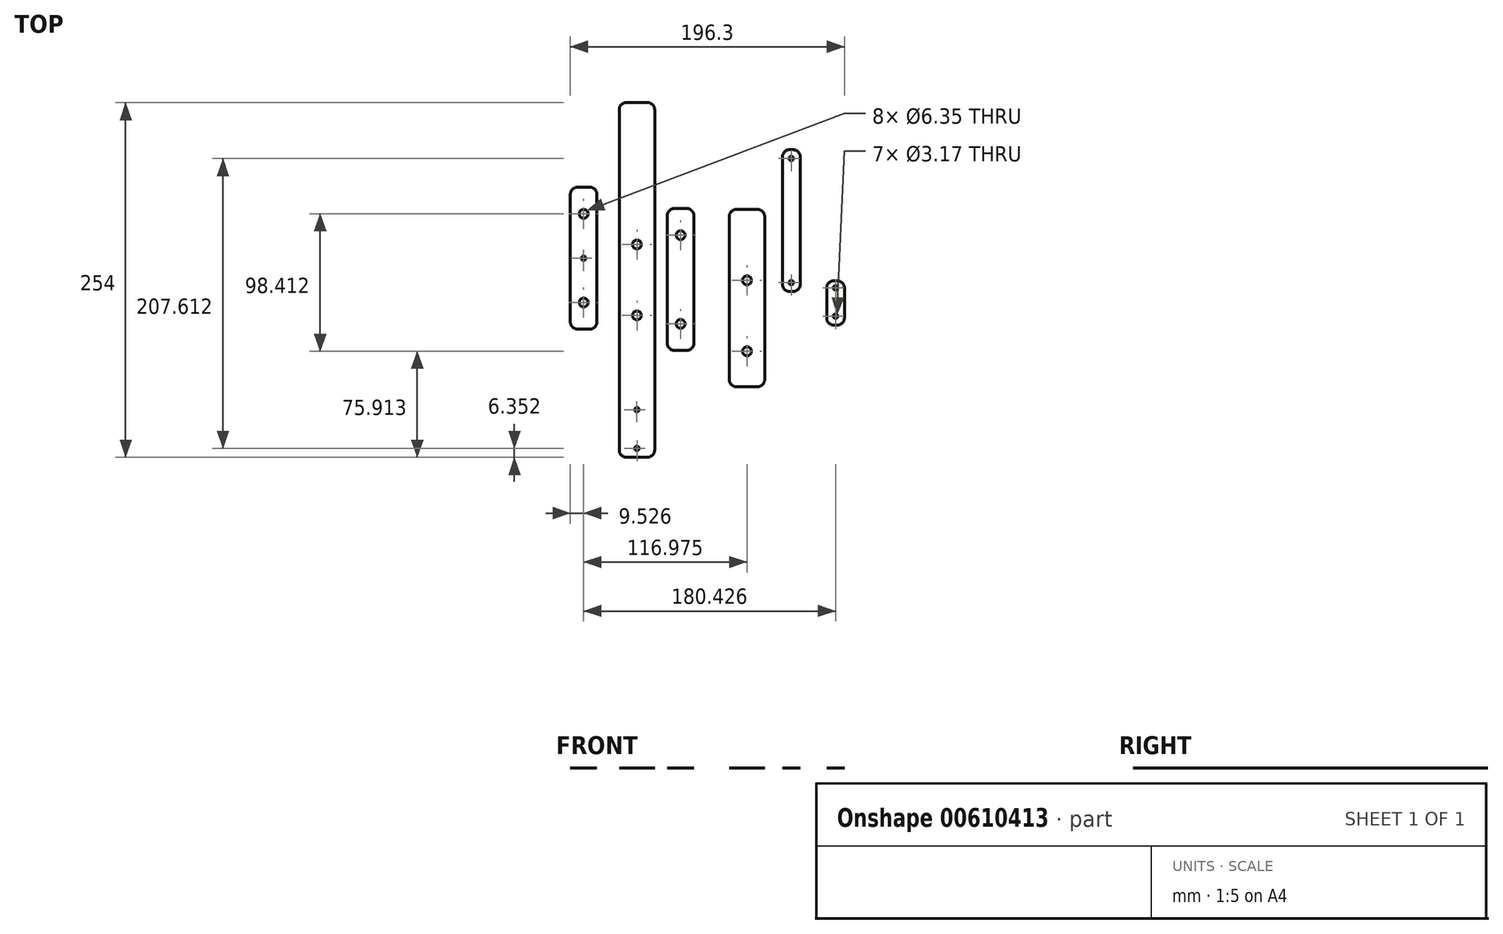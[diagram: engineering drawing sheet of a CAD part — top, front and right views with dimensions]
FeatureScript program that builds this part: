
annotation { "Feature Type Name" : "Feature", "Feature Type Description" : "" }
export const myFeature = defineFeature(function(context is Context, id is Id, definition is map)
    precondition{}
    {
        {
            var Q0;
            Q0=qCreatedBy(makeId("Top.planeOp"),FACE);
            var sketch = newSketch(context, id + "F0", { "sketchPlane" : qUnion([Q0])});
            skLineSegment(sketch, "E0.bottom", {"start": v(-140.54, 177.2) * mm, "end": v(-125.3, 177.2) * mm});
            skLineSegment(sketch, "E0.top", {"start": v(-140.54, -76.8) * mm, "end": v(-125.3, -76.8) * mm});
            skLineSegment(sketch, "E0.left", {"start": v(-145.62, 172.12) * mm, "end": v(-145.62, -71.72) * mm});
            skLineSegment(sketch, "E0.right", {"start": v(-120.22, 172.12) * mm, "end": v(-120.22, -71.72) * mm});
            skCircle(sketch, "E1", {"center": v(-132.92, 24.8) * mm, "radius": 3.18 * mm});
            skCircle(sketch, "E2", {"center": v(-132.92, 75.6) * mm, "radius": 3.18 * mm});
            skCircle(sketch, "E3", {"center": v(-132.92, -70.45) * mm, "radius": 1.59 * mm});
            skPoint(sketch, "E3.centerSnap0", {"position": v(-132.92, -76.8) * mm});
            skCircle(sketch, "E4", {"center": v(-132.95, -42.69) * mm, "radius": 1.59 * mm});
            skPoint(sketch, "E5.visualSharp", {"position": v(-145.62, 177.2) * mm});
            skArc(sketch, "E5.filletArc", {"start": v(-140.54, 177.2) * mm, "mid": v(-144.14, 175.71) * mm, "end": v(-145.62, 172.12) * mm});
            skPoint(sketch, "E6.visualSharp", {"position": v(-120.22, 177.2) * mm});
            skArc(sketch, "E6.filletArc", {"start": v(-120.22, 172.12) * mm, "mid": v(-121.71, 175.71) * mm, "end": v(-125.3, 177.2) * mm});
            skPoint(sketch, "E7.visualSharp", {"position": v(-145.62, -76.8) * mm});
            skArc(sketch, "E7.filletArc", {"start": v(-145.62, -71.72) * mm, "mid": v(-144.14, -75.31) * mm, "end": v(-140.54, -76.8) * mm});
            skPoint(sketch, "E8.visualSharp", {"position": v(-120.22, -76.8) * mm});
            skArc(sketch, "E8.filletArc", {"start": v(-125.3, -76.8) * mm, "mid": v(-121.71, -75.31) * mm, "end": v(-120.22, -71.72) * mm});
            skSolve(sketch);
        }
        {
            var Q0;
            Q0=qCreatedBy(makeId("Top.planeOp"),FACE);
            var sketch = newSketch(context, id + "F1", { "sketchPlane" : qUnion([Q0])});
            skLineSegment(sketch, "E9.bottom", {"start": v(-61.74, 100.71) * mm, "end": v(-46.5, 100.71) * mm});
            skLineSegment(sketch, "E9.top", {"start": v(-61.74, -26.29) * mm, "end": v(-46.5, -26.29) * mm});
            skLineSegment(sketch, "E9.left", {"start": v(-66.82, 95.63) * mm, "end": v(-66.82, -21.2) * mm});
            skLineSegment(sketch, "E9.right", {"start": v(-41.42, 95.63) * mm, "end": v(-41.42, -21.2) * mm});
            skCircle(sketch, "E10", {"center": v(-54.12, 49.91) * mm, "radius": 3.18 * mm});
            skCircle(sketch, "E11", {"center": v(-54.12, -0.89) * mm, "radius": 3.18 * mm});
            skPoint(sketch, "E12.visualSharp", {"position": v(-66.82, 100.71) * mm});
            skArc(sketch, "E12.filletArc", {"start": v(-61.74, 100.71) * mm, "mid": v(-65.33, 99.23) * mm, "end": v(-66.82, 95.63) * mm});
            skPoint(sketch, "E13.visualSharp", {"position": v(-41.42, 100.71) * mm});
            skArc(sketch, "E13.filletArc", {"start": v(-41.42, 95.63) * mm, "mid": v(-42.9, 99.23) * mm, "end": v(-46.5, 100.71) * mm});
            skPoint(sketch, "E14.visualSharp", {"position": v(-66.82, -26.29) * mm});
            skArc(sketch, "E14.filletArc", {"start": v(-66.82, -21.2) * mm, "mid": v(-65.33, -24.8) * mm, "end": v(-61.74, -26.29) * mm});
            skPoint(sketch, "E15.visualSharp", {"position": v(-41.42, -26.29) * mm});
            skArc(sketch, "E15.filletArc", {"start": v(-46.5, -26.29) * mm, "mid": v(-42.9, -24.8) * mm, "end": v(-41.42, -21.2) * mm});
            skSolve(sketch);
        }
        {
            var Q0;
            Q0=qCreatedBy(makeId("Top.planeOp"),FACE);
            var sketch = newSketch(context, id + "F2", { "sketchPlane" : qUnion([Q0])});
            skLineSegment(sketch, "E16.bottom", {"start": v(-106.08, 101.31) * mm, "end": v(-97.19, 101.31) * mm});
            skLineSegment(sketch, "E16.top", {"start": v(-106.08, -0.29) * mm, "end": v(-97.19, -0.29) * mm});
            skLineSegment(sketch, "E16.left", {"start": v(-111.16, 96.23) * mm, "end": v(-111.16, 4.8) * mm});
            skLineSegment(sketch, "E16.right", {"start": v(-92.1, 96.23) * mm, "end": v(-92.1, 4.8) * mm});
            skCircle(sketch, "E17", {"center": v(-101.63, 82.26) * mm, "radius": 3.18 * mm});
            skCircle(sketch, "E18", {"center": v(-101.63, 18.76) * mm, "radius": 3.18 * mm});
            skPoint(sketch, "E19.visualSharp", {"position": v(-111.16, 101.31) * mm});
            skArc(sketch, "E19.filletArc", {"start": v(-106.08, 101.31) * mm, "mid": v(-109.67, 99.83) * mm, "end": v(-111.16, 96.23) * mm});
            skPoint(sketch, "E20.visualSharp", {"position": v(-92.1, 101.31) * mm});
            skArc(sketch, "E20.filletArc", {"start": v(-92.1, 96.23) * mm, "mid": v(-93.6, 99.83) * mm, "end": v(-97.19, 101.31) * mm});
            skPoint(sketch, "E21.visualSharp", {"position": v(-111.16, -0.29) * mm});
            skArc(sketch, "E21.filletArc", {"start": v(-111.16, 4.8) * mm, "mid": v(-109.67, 1.2) * mm, "end": v(-106.08, -0.29) * mm});
            skPoint(sketch, "E22.visualSharp", {"position": v(-92.1, -0.29) * mm});
            skArc(sketch, "E22.filletArc", {"start": v(-97.19, -0.29) * mm, "mid": v(-93.6, 1.2) * mm, "end": v(-92.1, 4.8) * mm});
            skSolve(sketch);
        }
        {
            var Q0;
            Q0=qCreatedBy(makeId("Top.planeOp"),FACE);
            var sketch = newSketch(context, id + "F3", { "sketchPlane" : qUnion([Q0])});
            skLineSegment(sketch, "E23.bottom", {"start": v(-23.62, 143.51) * mm, "end": v(-21.08, 143.51) * mm});
            skLineSegment(sketch, "E23.top", {"start": v(-23.62, 41.91) * mm, "end": v(-21.08, 41.91) * mm});
            skLineSegment(sketch, "E23.left", {"start": v(-28.7, 138.43) * mm, "end": v(-28.7, 47) * mm});
            skLineSegment(sketch, "E23.right", {"start": v(-16, 138.43) * mm, "end": v(-16, 47) * mm});
            skCircle(sketch, "E24", {"center": v(-22.35, 48.26) * mm, "radius": 1.59 * mm});
            skCircle(sketch, "E25", {"center": v(-22.35, 137.16) * mm, "radius": 1.59 * mm});
            skPoint(sketch, "E26.visualSharp", {"position": v(-28.7, 143.51) * mm});
            skArc(sketch, "E26.filletArc", {"start": v(-23.62, 143.51) * mm, "mid": v(-27.2, 142.03) * mm, "end": v(-28.7, 138.43) * mm});
            skPoint(sketch, "E27.visualSharp", {"position": v(-16, 143.51) * mm});
            skArc(sketch, "E27.filletArc", {"start": v(-16, 138.43) * mm, "mid": v(-17.48, 142.03) * mm, "end": v(-21.08, 143.51) * mm});
            skPoint(sketch, "E28.visualSharp", {"position": v(-28.7, 41.91) * mm});
            skArc(sketch, "E28.filletArc", {"start": v(-28.7, 47) * mm, "mid": v(-27.2, 43.4) * mm, "end": v(-23.62, 41.91) * mm});
            skPoint(sketch, "E29.visualSharp", {"position": v(-16, 41.91) * mm});
            skArc(sketch, "E29.filletArc", {"start": v(-21.08, 41.91) * mm, "mid": v(-17.48, 43.4) * mm, "end": v(-16, 47) * mm});
            skSolve(sketch);
        }
        {
            var Q0;
            Q0=qCreatedBy(makeId("Top.planeOp"),FACE);
            var sketch = newSketch(context, id + "F4", { "sketchPlane" : qUnion([Q0])});
            skLineSegment(sketch, "E30.bottom", {"start": v(-175.54, 116.57) * mm, "end": v(-166.65, 116.57) * mm});
            skLineSegment(sketch, "E30.top", {"start": v(-175.54, 14.97) * mm, "end": v(-166.65, 14.97) * mm});
            skLineSegment(sketch, "E30.left", {"start": v(-180.62, 111.5) * mm, "end": v(-180.62, 20.05) * mm});
            skLineSegment(sketch, "E30.right", {"start": v(-161.57, 111.5) * mm, "end": v(-161.57, 20.05) * mm});
            skCircle(sketch, "E31", {"center": v(-171.1, 97.52) * mm, "radius": 3.18 * mm});
            skCircle(sketch, "E32", {"center": v(-171.1, 34.02) * mm, "radius": 3.18 * mm});
            skCircle(sketch, "E33", {"center": v(-171.1, 65.77) * mm, "radius": 1.59 * mm});
            skPoint(sketch, "E34.visualSharp", {"position": v(-180.62, 116.57) * mm});
            skArc(sketch, "E34.filletArc", {"start": v(-175.54, 116.57) * mm, "mid": v(-179.13, 115.09) * mm, "end": v(-180.62, 111.5) * mm});
            skPoint(sketch, "E35.visualSharp", {"position": v(-161.57, 116.57) * mm});
            skArc(sketch, "E35.filletArc", {"start": v(-161.57, 111.5) * mm, "mid": v(-163.06, 115.09) * mm, "end": v(-166.65, 116.57) * mm});
            skPoint(sketch, "E36.visualSharp", {"position": v(-180.62, 14.97) * mm});
            skArc(sketch, "E36.filletArc", {"start": v(-180.62, 20.05) * mm, "mid": v(-179.13, 16.46) * mm, "end": v(-175.54, 14.97) * mm});
            skPoint(sketch, "E37.visualSharp", {"position": v(-161.57, 14.97) * mm});
            skArc(sketch, "E37.filletArc", {"start": v(-166.65, 14.97) * mm, "mid": v(-163.06, 16.46) * mm, "end": v(-161.57, 20.05) * mm});
            skSolve(sketch);
        }
        {
            var Q0;
            Q0=qCreatedBy(makeId("Top.planeOp"),FACE);
            var sketch = newSketch(context, id + "F5", { "sketchPlane" : qUnion([Q0])});
            skCircle(sketch, "E38", {"center": v(9.33, 24.2) * mm, "radius": 1.59 * mm});
            skLineSegment(sketch, "E39", {"start": v(9.33, 17.84) * mm, "end": v(9.33, 49.6) * mm, "construction": true});
            skCircle(sketch, "E40", {"center": v(9.33, 44.51) * mm, "radius": 1.59 * mm});
            skLineSegment(sketch, "E41.bottom", {"start": v(8.06, 49.6) * mm, "end": v(10.6, 49.6) * mm});
            skLineSegment(sketch, "E41.top", {"start": v(8.06, 17.84) * mm, "end": v(10.6, 17.84) * mm});
            skLineSegment(sketch, "E41.left", {"start": v(2.98, 44.51) * mm, "end": v(2.98, 22.92) * mm});
            skLineSegment(sketch, "E41.right", {"start": v(15.68, 44.51) * mm, "end": v(15.68, 22.92) * mm});
            skPoint(sketch, "E42.visualSharp", {"position": v(2.98, 49.6) * mm});
            skArc(sketch, "E42.filletArc", {"start": v(8.06, 49.6) * mm, "mid": v(4.47, 48.1) * mm, "end": v(2.98, 44.51) * mm});
            skPoint(sketch, "E43.visualSharp", {"position": v(15.68, 49.6) * mm});
            skArc(sketch, "E43.filletArc", {"start": v(15.68, 44.51) * mm, "mid": v(14.2, 48.1) * mm, "end": v(10.6, 49.6) * mm});
            skPoint(sketch, "E44.visualSharp", {"position": v(2.98, 17.84) * mm});
            skArc(sketch, "E44.filletArc", {"start": v(2.98, 22.92) * mm, "mid": v(4.47, 19.33) * mm, "end": v(8.06, 17.84) * mm});
            skPoint(sketch, "E45.visualSharp", {"position": v(15.68, 17.84) * mm});
            skArc(sketch, "E45.filletArc", {"start": v(10.6, 17.84) * mm, "mid": v(14.2, 19.33) * mm, "end": v(15.68, 22.92) * mm});
            skSolve(sketch);
        }
        {
            var Q0;
            Q0=makeQuery(id+"F0.imprint","IMPRINT",FACE,{"disambiguationData":[TD([[makeQuery(id+"F0.imprint","IMPRINT",EDGE,{"derivedFrom":sQuery(id+"F0.wireOp",EDGE,"E0.bottom")}),-1.0]])]});
            extrude(context, id + "F6", {"entities" : qUnion([Q0]), "depth" : 1 / 203.2 * mm, "offsetDistance" : 25.4 * mm});
        }
        {
            var Q0;
            Q0=makeQuery(id+"F2.imprint","IMPRINT",FACE,{"disambiguationData":[TD([[makeQuery(id+"F2.imprint","IMPRINT",EDGE,{"derivedFrom":sQuery(id+"F2.wireOp",EDGE,"E16.bottom")}),-1.0]])]});
            extrude(context, id + "F7", {"entities" : qUnion([Q0]), "depth" : 1 / 203.2 * mm, "offsetDistance" : 25.4 * mm});
        }
        {
            var Q0;
            Q0=makeQuery(id+"F1.imprint","IMPRINT",FACE,{"disambiguationData":[TD([[makeQuery(id+"F1.imprint","IMPRINT",EDGE,{"derivedFrom":sQuery(id+"F1.wireOp",EDGE,"E9.bottom")}),-1.0]])]});
            extrude(context, id + "F8", {"entities" : qUnion([Q0]), "depth" : 1 / 203.2 * mm, "offsetDistance" : 25.4 * mm});
        }
        {
            var Q0;
            Q0=makeQuery(id+"F3.imprint","IMPRINT",FACE,{"disambiguationData":[TD([[makeQuery(id+"F3.imprint","IMPRINT",EDGE,{"derivedFrom":sQuery(id+"F3.wireOp",EDGE,"E23.bottom")}),-1.0]])]});
            extrude(context, id + "F9", {"entities" : qUnion([Q0]), "depth" : 1 / 203.2 * mm, "offsetDistance" : 25.4 * mm});
        }
        {
            var Q0;
            Q0=makeQuery(id+"F4.imprint","IMPRINT",FACE,{"disambiguationData":[TD([[makeQuery(id+"F4.imprint","IMPRINT",EDGE,{"derivedFrom":sQuery(id+"F4.wireOp",EDGE,"E30.bottom")}),-1.0]])]});
            extrude(context, id + "F10", {"entities" : qUnion([Q0]), "depth" : 1 / 203.2 * mm, "offsetDistance" : 25.4 * mm});
        }
        {
            var Q0;
            Q0=makeQuery(id+"F5.imprint","IMPRINT",FACE,{"disambiguationData":[TD([[makeQuery(id+"F5.imprint","IMPRINT",EDGE,{"derivedFrom":sQuery(id+"F5.wireOp",EDGE,"AHBCslwo-ywr5-xoyd-0ShM-mktcgXGJmMpd")}),1.0]])]});
            var Q1;
            Q1=makeQuery(id+"F5.imprint","IMPRINT",FACE,{"disambiguationData":[TD([[makeQuery(id+"F5.imprint","IMPRINT",EDGE,{"derivedFrom":sQuery(id+"F5.wireOp",EDGE,"E38")}),-1.0]])]});
            extrude(context, id + "F11", {"entities" : qUnion([Q0, Q1]), "depth" : 1 / 203.2 * mm, "offsetDistance" : 25.4 * mm});
        }
    });
